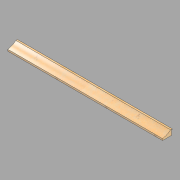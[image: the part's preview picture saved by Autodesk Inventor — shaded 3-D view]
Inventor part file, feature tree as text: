
AUTODESK INVENTOR PART (.ipt)
format: ipt  version: 2022.2 (Build 262287010, 287A)  size: 121,856 bytes
history: native  units: in
note: dims shown in document units (in); Inventor stores cm internally (conversion verified against a paired STEP export)
features: revolve x2, direct_edit x1, other x1
ambient origin geometry x8: Origin, YZ Plane, XZ Plane, XY Plane, X Axis, Y Axis, Z Axis, Center Point
bodies: Solid1 (feature_tree)
feature tree (4):
  direct_edit  "Direct Edit1"
  other  "Upper Jamb (1) (1)"
  revolve  "Rotate1"  [1 undecoded]
  revolve  "Rotate2"  [1 undecoded]
note: 2 required parameter values undecoded (feature->parameter linkage not recoverable at this tier; creation-order binding heuristic only, values carry confidence <= 0.55)
